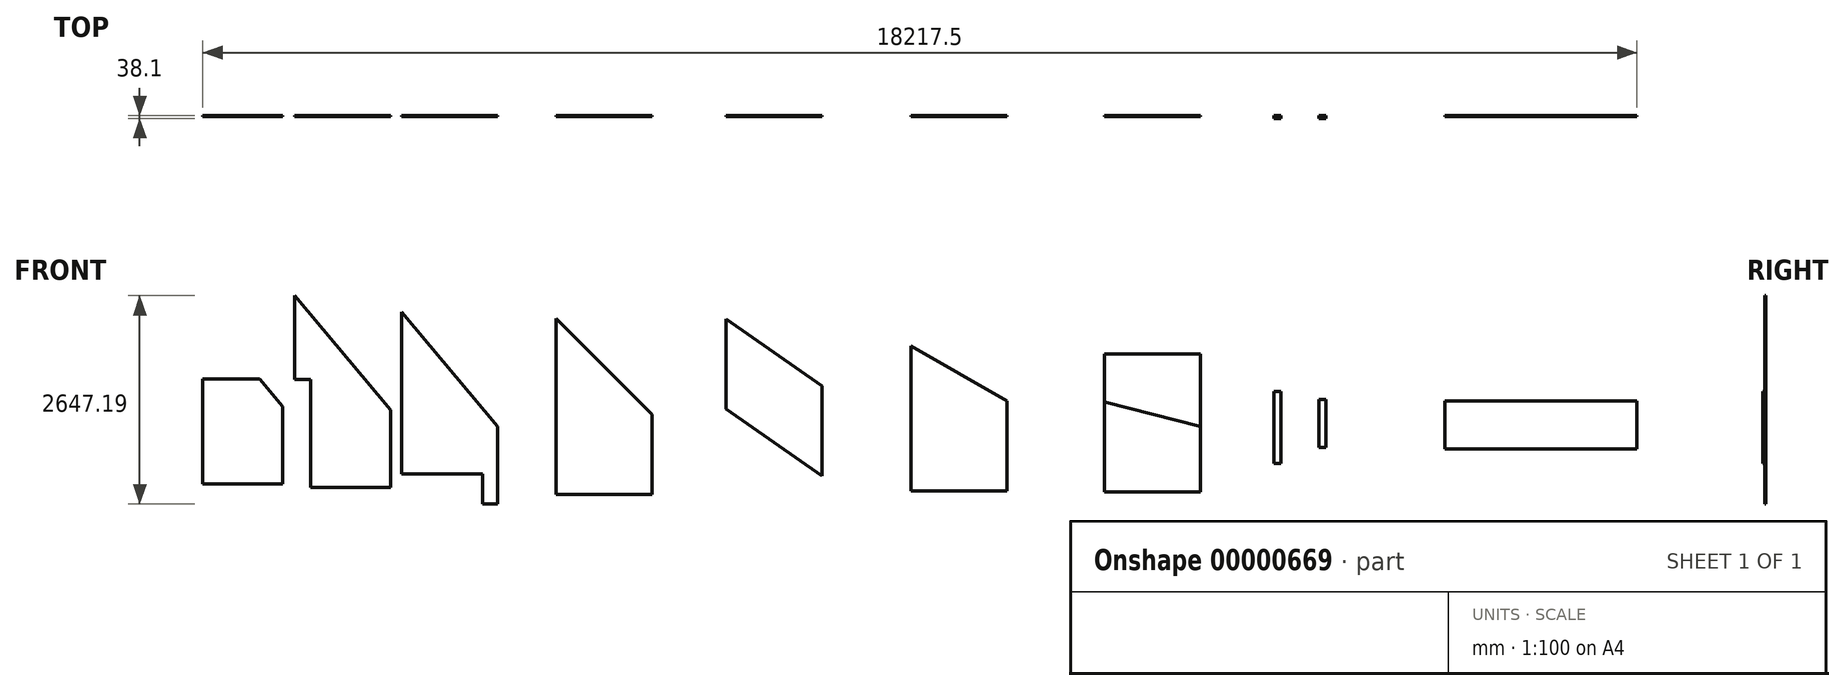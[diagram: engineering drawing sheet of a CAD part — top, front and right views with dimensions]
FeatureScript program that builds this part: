
annotation { "Feature Type Name" : "Feature", "Feature Type Description" : "" }
export const myFeature = defineFeature(function(context is Context, id is Id, definition is map)
    precondition{}
    {
        {
            var Q0;
            Q0=qCreatedBy(makeId("Front.planeOp"),FACE);
            var sketch = newSketch(context, id + "F0", { "sketchPlane" : qUnion([Q0])});
            skLineSegment(sketch, "E0.bottom", {"start": v(-663, 1340.6) * mm, "end": v(556.2, 1340.6) * mm});
            skLineSegment(sketch, "E0.top", {"start": v(-663, -1097.8) * mm, "end": v(556.2, -1097.8) * mm});
            skLineSegment(sketch, "E0.left", {"start": v(-663, 1340.6) * mm, "end": v(-663, -1097.8) * mm});
            skLineSegment(sketch, "E0.right", {"start": v(556.2, 1340.6) * mm, "end": v(556.2, -1097.8) * mm});
            skLineSegment(sketch, "E1", {"start": v(-663, 1340.6) * mm, "end": v(556.2, -112.38) * mm});
            skLineSegment(sketch, "E2", {"start": v(-663, 273.8) * mm, "end": v(-459.8, 273.8) * mm});
            skLineSegment(sketch, "E3", {"start": v(-459.8, 273.8) * mm, "end": v(-459.8, -1097.8) * mm});
            skLineSegment(sketch, "E4", {"start": v(-459.8, -1097.8) * mm, "end": v(556.2, -1097.8) * mm});
            skSolve(sketch);
        }
        {
            var Q0;
            {var subQ2=sQuery(id+"F0.wireOp",EDGE,"E1");Q0=makeQuery(id+"F0.imprint","IMPRINT",FACE,{"disambiguationData":[TD([[makeQuery(id+"F0.imprint","IMPRINT",EDGE,{"derivedFrom":subQ2}),-1.0]])]});}
            extrude(context, id + "F1", {"entities" : qUnion([Q0]), "depth" : 12.7 * mm});
        }
        {
            var Q0;
            Q0=qCreatedBy(makeId("Front.planeOp"),FACE);
            var sketch = newSketch(context, id + "F2", { "sketchPlane" : qUnion([Q0])});
            skLineSegment(sketch, "E5.bottom", {"start": v(692.98, 1131.82) * mm, "end": v(1912.18, 1131.82) * mm});
            skLineSegment(sketch, "E5.top", {"start": v(692.98, -1306.58) * mm, "end": v(1912.18, -1306.58) * mm});
            skLineSegment(sketch, "E5.left", {"start": v(692.98, 1131.82) * mm, "end": v(692.98, -1306.58) * mm});
            skLineSegment(sketch, "E5.right", {"start": v(1912.18, 1131.82) * mm, "end": v(1912.18, -1306.58) * mm});
            skLineSegment(sketch, "E6", {"start": v(692.98, 1131.82) * mm, "end": v(1912.18, -321.17) * mm});
            skLineSegment(sketch, "E7", {"start": v(692.98, -925.58) * mm, "end": v(1721.68, -925.58) * mm});
            skLineSegment(sketch, "E8", {"start": v(1721.68, -925.58) * mm, "end": v(1721.68, -1306.58) * mm});
            skSolve(sketch);
        }
        {
            var Q0;
            {var subQ2=sQuery(id+"F2.wireOp",EDGE,"E6");Q0=makeQuery(id+"F2.imprint","IMPRINT",FACE,{"disambiguationData":[TD([[makeQuery(id+"F2.imprint","IMPRINT",EDGE,{"derivedFrom":subQ2}),-1.0]])]});}
            extrude(context, id + "F3", {"entities" : qUnion([Q0]), "depth" : 12.7 * mm});
        }
        {
            var Q0;
            Q0=qCreatedBy(makeId("Front.planeOp"),FACE);
            var sketch = newSketch(context, id + "F4", { "sketchPlane" : qUnion([Q0])});
            skLineSegment(sketch, "E9.bottom", {"start": v(2654.54, 1049.95) * mm, "end": v(3873.74, 1049.95) * mm});
            skLineSegment(sketch, "E9.top", {"start": v(2654.54, -1388.45) * mm, "end": v(3873.74, -1388.45) * mm});
            skLineSegment(sketch, "E9.left", {"start": v(2654.54, 1049.95) * mm, "end": v(2654.54, -1388.45) * mm});
            skLineSegment(sketch, "E9.right", {"start": v(3873.74, 1049.95) * mm, "end": v(3873.74, -1388.45) * mm});
            skLineSegment(sketch, "E10", {"start": v(2654.54, 1049.95) * mm, "end": v(3873.74, -169.25) * mm});
            skLineSegment(sketch, "E11", {"start": v(2654.54, -1185.25) * mm, "end": v(3873.74, -1185.25) * mm});
            skSolve(sketch);
        }
        {
            var Q0;
            {var subQ1=sQuery(id+"F4.wireOp",EDGE,"E10");Q0=makeQuery(id+"F4.imprint","IMPRINT",FACE,{"disambiguationData":[TD([[makeQuery(id+"F4.imprint","IMPRINT",EDGE,{"derivedFrom":subQ1}),-1.0]])]});}
            extrude(context, id + "F5", {"entities" : qUnion([Q0]), "depth" : 12.7 * mm});
        }
        {
            var Q0;
            Q0=qCreatedBy(makeId("Front.planeOp"),FACE);
            var sketch = newSketch(context, id + "F6", { "sketchPlane" : qUnion([Q0])});
            skLineSegment(sketch, "E12.bottom", {"start": v(4817.1, 1044.26) * mm, "end": v(6036.3, 1044.26) * mm});
            skLineSegment(sketch, "E12.top", {"start": v(4817.1, -1394.14) * mm, "end": v(6036.3, -1394.14) * mm});
            skLineSegment(sketch, "E12.left", {"start": v(4817.1, 1044.26) * mm, "end": v(4817.1, -1394.14) * mm});
            skLineSegment(sketch, "E12.right", {"start": v(6036.3, 1044.26) * mm, "end": v(6036.3, -1394.14) * mm});
            skLineSegment(sketch, "E13", {"start": v(4817.1, 1044.26) * mm, "end": v(6036.3, 190.57) * mm});
            skLineSegment(sketch, "E14", {"start": v(4817.1, -98.74) * mm, "end": v(6036.3, -952.43) * mm});
            skSolve(sketch);
        }
        {
            var Q0;
            {var subQ1=sQuery(id+"F6.wireOp",EDGE,"E13");Q0=makeQuery(id+"F6.imprint","IMPRINT",FACE,{"disambiguationData":[TD([[makeQuery(id+"F6.imprint","IMPRINT",EDGE,{"derivedFrom":subQ1}),-1.0]])]});}
            extrude(context, id + "F7", {"entities" : qUnion([Q0]), "depth" : 12.7 * mm});
        }
        {
            var Q0;
            Q0=qCreatedBy(makeId("Front.planeOp"),FACE);
            var sketch = newSketch(context, id + "F8", { "sketchPlane" : qUnion([Q0])});
            skLineSegment(sketch, "E15.bottom", {"start": v(7162.18, 703.82) * mm, "end": v(8381.38, 703.82) * mm});
            skLineSegment(sketch, "E15.top", {"start": v(7162.18, -1734.58) * mm, "end": v(8381.38, -1734.58) * mm});
            skLineSegment(sketch, "E15.left", {"start": v(7162.18, 703.82) * mm, "end": v(7162.18, -1734.58) * mm});
            skLineSegment(sketch, "E15.right", {"start": v(8381.38, 703.82) * mm, "end": v(8381.38, -1734.58) * mm});
            skLineSegment(sketch, "E16", {"start": v(7162.18, -1137.68) * mm, "end": v(8381.38, -1137.68) * mm});
            skLineSegment(sketch, "E17", {"start": v(7162.18, 703.82) * mm, "end": v(8381.38, -0.08) * mm});
            skSolve(sketch);
        }
        {
            var Q0;
            {var subQ1=sQuery(id+"F8.wireOp",EDGE,"E16");Q0=makeQuery(id+"F8.imprint","IMPRINT",FACE,{"disambiguationData":[TD([[makeQuery(id+"F8.imprint","IMPRINT",EDGE,{"derivedFrom":subQ1}),1.0]])]});}
            extrude(context, id + "F9", {"entities" : qUnion([Q0]), "depth" : 12.7 * mm});
        }
        {
            var Q0;
            Q0=qCreatedBy(makeId("Front.planeOp"),FACE);
            var sketch = newSketch(context, id + "F10", { "sketchPlane" : qUnion([Q0])});
            skLineSegment(sketch, "E18.bottom", {"start": v(-816.3, 1384.74) * mm, "end": v(-2035.5, 1384.74) * mm});
            skLineSegment(sketch, "E18.top", {"start": v(-816.3, -1053.66) * mm, "end": v(-2035.5, -1053.66) * mm});
            skLineSegment(sketch, "E18.left", {"start": v(-816.3, 1384.74) * mm, "end": v(-816.3, -1053.66) * mm});
            skLineSegment(sketch, "E18.right", {"start": v(-2035.5, 1384.74) * mm, "end": v(-2035.5, -1053.66) * mm});
            skLineSegment(sketch, "E19", {"start": v(-2035.5, 279.84) * mm, "end": v(-816.3, 279.84) * mm});
            skLineSegment(sketch, "E20", {"start": v(-2035.5, 1384.74) * mm, "end": v(-816.3, -68.25) * mm});
            skLineSegment(sketch, "E21", {"start": v(-1832.3, 279.84) * mm, "end": v(-1832.3, -1053.66) * mm});
            skSolve(sketch);
        }
        {
            var Q0;
            {var subQ0=sQuery(id+"F10.wireOp",EDGE,"E21");Q0=makeQuery(id+"F10.imprint","IMPRINT",FACE,{"disambiguationData":[TD([[makeQuery(id+"F10.imprint","IMPRINT",EDGE,{"derivedFrom":subQ0}),1.0]])]});}
            extrude(context, id + "F11", {"entities" : qUnion([Q0]), "depth" : 12.7 * mm});
        }
        {
            var Q0;
            Q0=qCreatedBy(makeId("Front.planeOp"),FACE);
            var sketch = newSketch(context, id + "F12", { "sketchPlane" : qUnion([Q0])});
            skLineSegment(sketch, "E22.bottom", {"start": v(9621.96, 1287.62) * mm, "end": v(10841.16, 1287.62) * mm});
            skLineSegment(sketch, "E22.top", {"start": v(9621.96, -1150.78) * mm, "end": v(10841.16, -1150.78) * mm});
            skLineSegment(sketch, "E22.left", {"start": v(9621.96, 1287.62) * mm, "end": v(9621.96, -1150.78) * mm});
            skLineSegment(sketch, "E22.right", {"start": v(10841.16, 1287.62) * mm, "end": v(10841.16, -1150.78) * mm});
            skLineSegment(sketch, "E23", {"start": v(9621.96, -7.78) * mm, "end": v(10841.16, -318.93) * mm});
            skLineSegment(sketch, "E24", {"start": v(9621.96, 601.82) * mm, "end": v(10841.16, 601.82) * mm});
            skSolve(sketch);
        }
        {
            var Q0;
            {var subQ2=sQuery(id+"F12.wireOp",EDGE,"E22.top");Q0=makeQuery(id+"F12.imprint","IMPRINT",FACE,{"disambiguationData":[TD([[makeQuery(id+"F12.imprint","IMPRINT",EDGE,{"derivedFrom":subQ2}),1.0]])]});}
            extrude(context, id + "F13", {"entities" : qUnion([Q0]), "depth" : 12.7 * mm});
        }
        {
            var Q0;
            Q0=qCreatedBy(makeId("Front.planeOp"),FACE);
            var sketch = newSketch(context, id + "F14", { "sketchPlane" : qUnion([Q0])});
            skLineSegment(sketch, "E25.bottom", {"start": v(11774.76, 123.7) * mm, "end": v(11863.66, 123.7) * mm});
            skLineSegment(sketch, "E25.top", {"start": v(11774.76, -790.7) * mm, "end": v(11863.66, -790.7) * mm});
            skLineSegment(sketch, "E25.left", {"start": v(11774.76, 123.7) * mm, "end": v(11774.76, -790.7) * mm});
            skLineSegment(sketch, "E25.right", {"start": v(11863.66, 123.7) * mm, "end": v(11863.66, -790.7) * mm});
            skSolve(sketch);
        }
        {
            var Q0;
            Q0=makeQuery(id+"F14.imprint","IMPRINT",FACE,{"disambiguationData":[TD([[makeQuery(id+"F14.imprint","IMPRINT",EDGE,{"derivedFrom":sQuery(id+"F14.wireOp",EDGE,"E25.bottom")}),-1.0]])]});
            extrude(context, id + "F15", {"entities" : qUnion([Q0]), "depth" : 38.1 * mm});
        }
        {
            var Q0;
            Q0=qCreatedBy(makeId("Front.planeOp"),FACE);
            var sketch = newSketch(context, id + "F16", { "sketchPlane" : qUnion([Q0])});
            skLineSegment(sketch, "E26.bottom", {"start": v(12345.2, 22.53) * mm, "end": v(12434.1, 22.53) * mm});
            skLineSegment(sketch, "E26.top", {"start": v(12345.2, -587.07) * mm, "end": v(12434.1, -587.07) * mm});
            skLineSegment(sketch, "E26.left", {"start": v(12345.2, 22.53) * mm, "end": v(12345.2, -587.07) * mm});
            skLineSegment(sketch, "E26.right", {"start": v(12434.1, 22.53) * mm, "end": v(12434.1, -587.07) * mm});
            skSolve(sketch);
        }
        {
            var Q0;
            Q0=makeQuery(id+"F16.imprint","IMPRINT",FACE,{"disambiguationData":[TD([[makeQuery(id+"F16.imprint","IMPRINT",EDGE,{"derivedFrom":sQuery(id+"F16.wireOp",EDGE,"E26.bottom")}),-1.0]])]});
            extrude(context, id + "F17", {"entities" : qUnion([Q0]), "depth" : 38.1 * mm});
        }
        {
            var Q0;
            Q0=qCreatedBy(makeId("Front.planeOp"),FACE);
            var sketch = newSketch(context, id + "F18", { "sketchPlane" : qUnion([Q0])});
            skLineSegment(sketch, "E27.bottom", {"start": v(13946.78, 0) * mm, "end": v(16385.18, 0) * mm});
            skLineSegment(sketch, "E27.top", {"start": v(13946.78, -609.6) * mm, "end": v(16385.18, -609.6) * mm});
            skLineSegment(sketch, "E27.left", {"start": v(13946.78, 0) * mm, "end": v(13946.78, -609.6) * mm});
            skLineSegment(sketch, "E27.right", {"start": v(16385.18, 0) * mm, "end": v(16385.18, -609.6) * mm});
            skSolve(sketch);
        }
        {
            var Q0;
            Q0=makeQuery(id+"F18.imprint","IMPRINT",FACE,{"disambiguationData":[TD([[makeQuery(id+"F18.imprint","IMPRINT",EDGE,{"derivedFrom":sQuery(id+"F18.wireOp",EDGE,"E27.bottom")}),-1.0]])]});
            extrude(context, id + "F19", {"entities" : qUnion([Q0]), "depth" : 12.7 * mm});
        }
        {
            var Q0;
            {var subQ1=sQuery(id+"F12.wireOp",EDGE,"E23");Q0=makeQuery(id+"F12.imprint","IMPRINT",FACE,{"disambiguationData":[TD([[makeQuery(id+"F12.imprint","IMPRINT",EDGE,{"derivedFrom":subQ1}),1.0]])]});}
            extrude(context, id + "F20", {"entities" : qUnion([Q0]), "depth" : 12.7 * mm});
        }
    });
